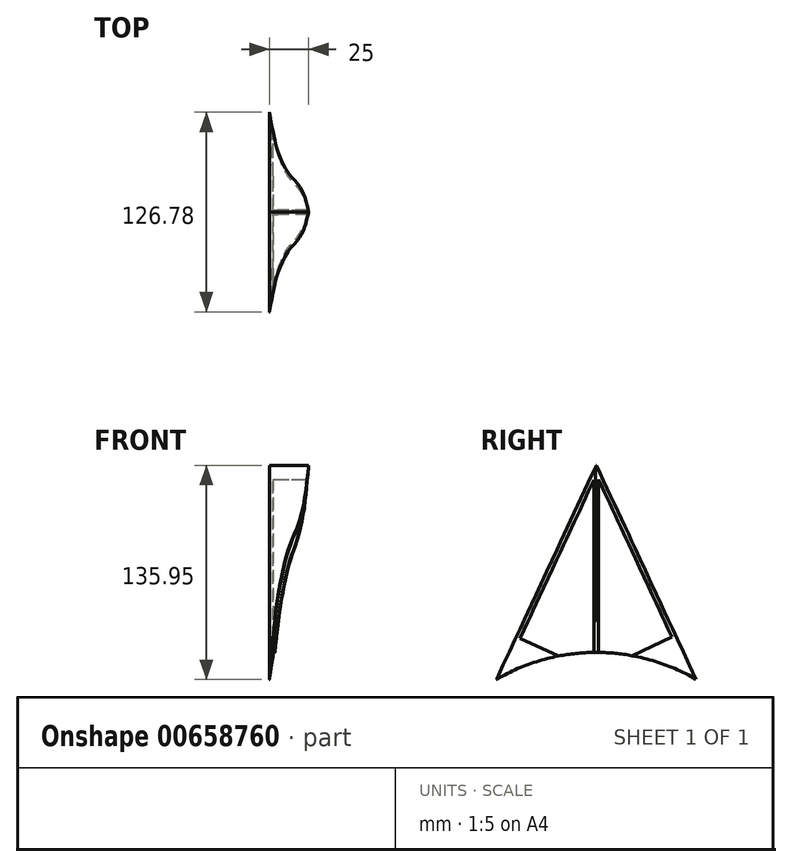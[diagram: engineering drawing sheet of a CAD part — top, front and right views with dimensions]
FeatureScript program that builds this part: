
annotation { "Feature Type Name" : "Feature", "Feature Type Description" : "" }
export const myFeature = defineFeature(function(context is Context, id is Id, definition is map)
    precondition{}
    {
        {
            var Q0;
            Q0=qCreatedBy(makeId("Right.planeOp"),FACE);
            var sketch = newSketch(context, id + "F0", { "sketchPlane" : qUnion([Q0])});
            skLineSegment(sketch, "E0", {"start": v(-63.4, -46.91) * mm, "end": v(0, 89.04) * mm});
            skLineSegment(sketch, "E1", {"start": v(0, 89.04) * mm, "end": v(63.4, -46.91) * mm});
            skArc(sketch, "E2", {"start": v(63.4, -46.91) * mm, "mid": v(0, -29.8) * mm, "end": v(-63.4, -46.91) * mm});
            skSolve(sketch);
        }
        {
            var Q0;
            Q0=makeQuery(id+"F0.imprint","IMPRINT",FACE,{"disambiguationData":[TD([[makeQuery(id+"F0.imprint","IMPRINT",EDGE,{"derivedFrom":sQuery(id+"F0.wireOp",EDGE,"E0")}),-1.0]])]});
            extrude(context, id + "F1", {"entities" : qUnion([Q0]), "depth" : 25 * mm, "offsetDistance" : 25 * mm});
        }
        {
            var Q0;
            Q0=makeQuery(id+"F1.opExtrude","CAP_FACE",FACE,{"disambiguationData":[OSD([sQuery(id+"F0.wireOp",EDGE,"E0"),sQuery(id+"F0.wireOp",EDGE,"E1"),sQuery(id+"F0.wireOp",EDGE,"nNIfOJsI-hvlV-gdn3-kDpz-tTEKEMh6xaGT")])],"isStart":false});
            shell(context, id + "F2", {"entities" : qUnion([Q0]), "thickness" : 2.5 * mm});
        }
        {
            var Q0;
            Q0=makeQuery(id+"F2.opShell","OFFSET_FACE",FACE,{"disambiguationData":[OSD([sQuery(id+"F0.wireOp",EDGE,"E2")])]});
            var Q1;
            Q1=makeQuery(id+"F1.opExtrude","SWEPT_FACE",FACE,{"disambiguationData":[OSD([sQuery(id+"F0.wireOp",EDGE,"E2")])]});
            shell(context, id + "F3", {"entities" : qUnion([Q0, Q1]), "thickness" : 2.5 * mm});
        }
        {
            var Q0;
            Q0=makeQuery(id+"F1.opExtrude","CAP_FACE",FACE,{"disambiguationData":[OSD([sQuery(id+"F0.wireOp",EDGE,"E0"),sQuery(id+"F0.wireOp",EDGE,"E1"),sQuery(id+"F0.wireOp",EDGE,"E2")])],"isStart":false});
            var sketch = newSketch(context, id + "F4", { "sketchPlane" : qUnion([Q0])});
            skLineSegment(sketch, "E3", {"start": v(-55.54, -35.98) * mm, "end": v(-64.46, -55.1) * mm});
            skLineSegment(sketch, "E4", {"start": v(-64.46, -55.1) * mm, "end": v(57.92, -55.1) * mm});
            skLineSegment(sketch, "E5", {"start": v(57.92, -55.1) * mm, "end": v(63.4, -55.1) * mm});
            skLineSegment(sketch, "E6", {"start": v(63.4, -55.1) * mm, "end": v(57.92, -41.1) * mm});
            skLineSegment(sketch, "E7", {"start": v(57.92, -41.1) * mm, "end": v(52.14, -28.69) * mm});
            skLineSegment(sketch, "E8", {"start": v(52.14, -28.69) * mm, "end": v(35.89, -24.73) * mm});
            skLineSegment(sketch, "E9", {"start": v(35.89, -24.73) * mm, "end": v(-19.72, -17.76) * mm});
            skLineSegment(sketch, "E10", {"start": v(-19.72, -17.76) * mm, "end": v(-45.27, -26.74) * mm});
            skLineSegment(sketch, "E11", {"start": v(-45.27, -26.74) * mm, "end": v(-55.54, -35.98) * mm});
            skSolve(sketch);
        }
        {
            var Q0;
            Q0 = qSketchRegion(id + "F4", true);
            extrude(context, id + "F5", {"entities" : qUnion([Q0]), "operationType" : NewBodyOperationType.REMOVE, "oppositeDirection" : true, "depth" : 8.5 * mm, "offsetDistance" : 25 * mm});
        }
        {
            var Q0;
            Q0=makeQuery(id+"F1.opExtrude","CAP_FACE",FACE,{"disambiguationData":[OSD([sQuery(id+"F0.wireOp",EDGE,"E0"),sQuery(id+"F0.wireOp",EDGE,"E1"),sQuery(id+"F0.wireOp",EDGE,"E2")])],"isStart":false});
            var sketch = newSketch(context, id + "F6", { "sketchPlane" : qUnion([Q0])});
            skLineSegment(sketch, "E12", {"start": v(-1.64, -29.85) * mm, "end": v(-1.64, 83.12) * mm});
            skLineSegment(sketch, "E13", {"start": v(-1.64, 83.12) * mm, "end": v(0, 86.63) * mm});
            skLineSegment(sketch, "E14", {"start": v(0, 86.63) * mm, "end": v(1.39, 83.12) * mm});
            skLineSegment(sketch, "E15", {"start": v(1.39, 83.12) * mm, "end": v(1.39, -29.91) * mm});
            skLineSegment(sketch, "E16", {"start": v(1.39, -29.91) * mm, "end": v(-1.64, -29.85) * mm});
            skSolve(sketch);
        }
        {
            var Q0;
            Q0 = qSketchRegion(id + "F6", true);
            extrude(context, id + "F7", {"entities" : qUnion([Q0]), "operationType" : NewBodyOperationType.ADD, "oppositeDirection" : true, "depth" : 23 * mm, "offsetDistance" : 25 * mm});
        }
        {
            var Q0;
            Q0=makeQuery(id+"F1.opExtrude","SWEPT_FACE",FACE,{"disambiguationData":[OSD([sQuery(id+"F0.wireOp",EDGE,"E1")])]});
            var sketch = newSketch(context, id + "F8", { "sketchPlane" : qUnion([Q0])});
            skFitSpline(sketch, "E17", {"points": [v(0, -69.3) * mm, v(-3.2, -30.28) * mm, v(-5.03, -13.9) * mm, v(-11.28, 19.44) * mm, v(-17, 35.54) * mm, v(-21.18, 50.49) * mm, v(-23.4, 65.58) * mm, v(-25, 80.7) * mm], "startDerivative": vector(-18.2, 227.22) * mm, "endDerivative": vector(-12.8, 124.38) * mm});
            skLineSegment(sketch, "E18", {"start": v(-25, 80.7) * mm, "end": v(-25.87, 82.92) * mm});
            skLineSegment(sketch, "E19", {"start": v(-6.18, -81.71) * mm, "end": v(0, -69.3) * mm});
            skLineSegment(sketch, "E20", {"start": v(-25.87, 82.92) * mm, "end": v(-38.62, 75.67) * mm});
            skLineSegment(sketch, "E21", {"start": v(-38.62, 75.67) * mm, "end": v(-38.62, -82.03) * mm});
            skLineSegment(sketch, "E22", {"start": v(-38.62, -82.03) * mm, "end": v(-6.18, -81.71) * mm});
            skSolve(sketch);
        }
        {
            var Q0;
            Q0 = qSketchRegion(id + "F8", true);
            extrude(context, id + "F9", {"entities" : qUnion([Q0]), "operationType" : NewBodyOperationType.REMOVE, "oppositeDirection" : true, "depth" : 123.2 * mm, "offsetDistance" : 25 * mm});
        }
        {
            var Q0;
            Q0=makeQuery(id+"F1.opExtrude","SWEPT_FACE",FACE,{"disambiguationData":[OSD([sQuery(id+"F0.wireOp",EDGE,"E0")])]});
            var sketch = newSketch(context, id + "F10", { "sketchPlane" : qUnion([Q0])});
            skLineSegment(sketch, "E23", {"start": v(38.72, 76.07) * mm, "end": v(38.72, -81.63) * mm});
            skLineSegment(sketch, "E24.MirrorCS", {"start": v(25.97, 83.33) * mm, "end": v(38.72, 76.07) * mm});
            skFitSpline(sketch, "E25.MirrorCS", {"points": [v(0.1, -68.9) * mm, v(3.3, -29.87) * mm, v(5.13, -13.5) * mm, v(11.38, 19.85) * mm, v(17.11, 35.95) * mm, v(21.28, 50.9) * mm, v(23.5, 65.98) * mm, v(25.1, 81.1) * mm], "startDerivative": vector(18.2, 227.22) * mm, "endDerivative": vector(12.8, 124.38) * mm});
            skLineSegment(sketch, "E26.MirrorCS", {"start": v(38.72, -81.63) * mm, "end": v(6.28, -81.3) * mm});
            skLineSegment(sketch, "E27.MirrorCS", {"start": v(6.28, -81.3) * mm, "end": v(0.1, -68.9) * mm});
            skLineSegment(sketch, "E28", {"start": v(25.1, 81.1) * mm, "end": v(25.97, 83.33) * mm});
            skSolve(sketch);
        }
        {
            var Q0;
            Q0 = qSketchRegion(id + "F10", true);
            extrude(context, id + "F11", {"entities" : qUnion([Q0]), "operationType" : NewBodyOperationType.REMOVE, "oppositeDirection" : true, "depth" : 41 * mm, "offsetDistance" : 25 * mm});
        }
    });
